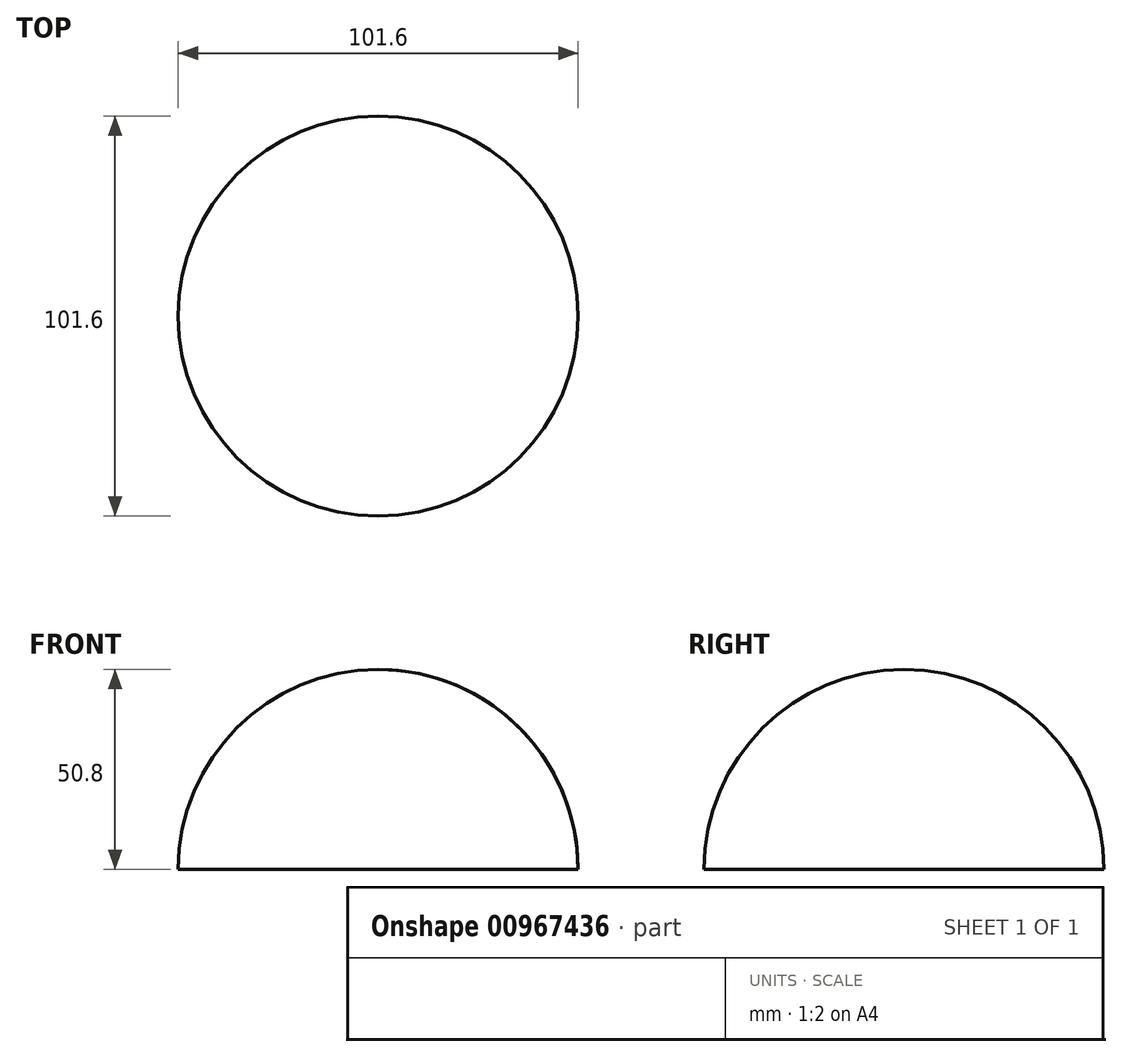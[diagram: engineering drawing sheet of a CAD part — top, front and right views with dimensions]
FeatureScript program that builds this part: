
annotation { "Feature Type Name" : "Feature", "Feature Type Description" : "" }
export const myFeature = defineFeature(function(context is Context, id is Id, definition is map)
    precondition{}
    {
        {
            var Q0;
            Q0=qCreatedBy(makeId("Front.planeOp"),FACE);
            var sketch = newSketch(context, id + "F0", { "sketchPlane" : qUnion([Q0])});
            skLineSegment(sketch, "E0", {"start": v(0, 0) * mm, "end": v(0, 50.8) * mm});
            skArc(sketch, "E1", {"start": v(0, 50.8) * mm, "mid": v(35.92, 35.92) * mm, "end": v(50.8, 0) * mm});
            skLineSegment(sketch, "E2", {"start": v(50.8, 0) * mm, "end": v(0, 0) * mm});
            skSolve(sketch);
        }
        {
            var Q0;
            Q0 = qSketchRegion(id + "F0", true);
            var Q1;
            Q1=sQuery(id+"F0.wireOp",EDGE,"E0");
            revolve(context, id + "F1", {"surfaceOperationType" : NewSurfaceOperationType.NEW, "entities" : qUnion([Q0]), "axis" : qUnion([Q1]), "revolveType" : RevolveType.FULL});
        }
    });
